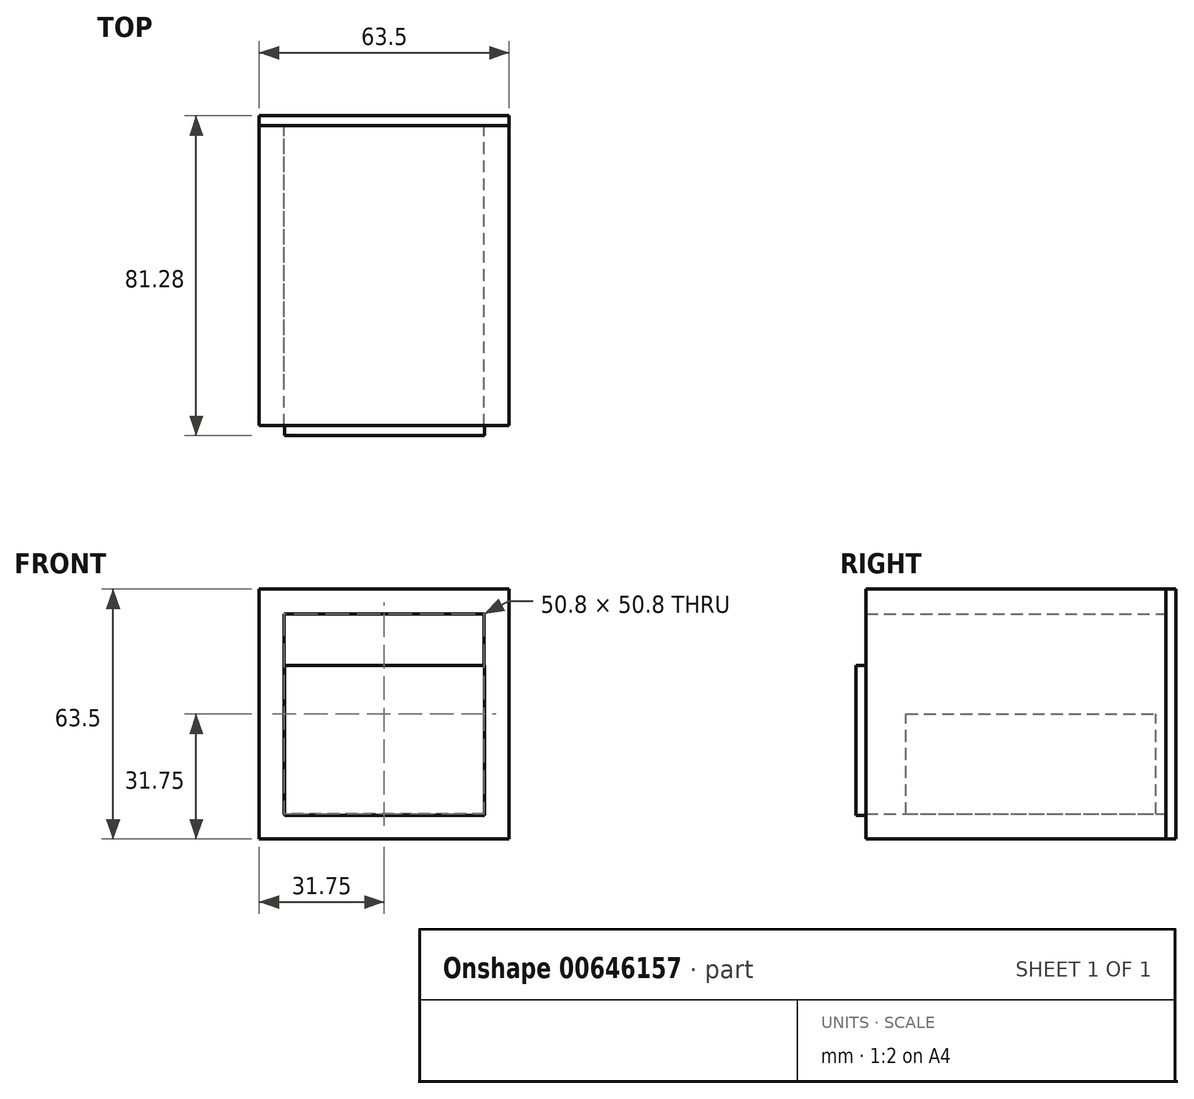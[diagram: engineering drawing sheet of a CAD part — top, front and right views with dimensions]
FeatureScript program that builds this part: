
annotation { "Feature Type Name" : "Feature", "Feature Type Description" : "" }
export const myFeature = defineFeature(function(context is Context, id is Id, definition is map)
    precondition{}
    {
        {
            var Q0;
            Q0=qCreatedBy(makeId("Front.planeOp"),FACE);
            var sketch = newSketch(context, id + "F0", { "sketchPlane" : qUnion([Q0])});
            skLineSegment(sketch, "E0.bottom", {"start": v(25.4, 25.4) * mm, "end": v(-25.4, 25.4) * mm});
            skLineSegment(sketch, "E0.top", {"start": v(25.4, -25.4) * mm, "end": v(-25.4, -25.4) * mm});
            skLineSegment(sketch, "E0.left", {"start": v(25.4, 25.4) * mm, "end": v(25.4, -25.4) * mm});
            skLineSegment(sketch, "E0.right", {"start": v(-25.4, 25.4) * mm, "end": v(-25.4, -25.4) * mm});
            skPoint(sketch, "E0.middle", {"position": v(0, 0) * mm});
            skSolve(sketch);
        }
        {
            var Q0;
            Q0=qCreatedBy(makeId("Front.planeOp"),FACE);
            var sketch = newSketch(context, id + "F1", { "sketchPlane" : qUnion([Q0])});
            skLineSegment(sketch, "E1.bottom", {"start": v(31.75, 31.75) * mm, "end": v(-31.75, 31.75) * mm});
            skLineSegment(sketch, "E1.top", {"start": v(31.75, -31.75) * mm, "end": v(-31.75, -31.75) * mm});
            skLineSegment(sketch, "E1.left", {"start": v(31.75, 31.75) * mm, "end": v(31.75, -31.75) * mm});
            skLineSegment(sketch, "E1.right", {"start": v(-31.75, 31.75) * mm, "end": v(-31.75, -31.75) * mm});
            skPoint(sketch, "E1.middle", {"position": v(0, 0) * mm});
            skSolve(sketch);
        }
        {
            var Q0;
            Q0=makeQuery(id+"F1.imprint","IMPRINT",FACE,{"disambiguationData":[TD([[makeQuery(id+"F1.imprint","IMPRINT",EDGE,{"derivedFrom":sQuery(id+"F1.wireOp",EDGE,"E1.bottom")}),1.0]])]});
            extrude(context, id + "F2", {"entities" : qUnion([Q0]), "depth" : 76.2 * mm, "offsetDistance" : 25.4 * mm});
        }
        {
            var Q0;
            Q0=qCreatedBy(makeId("Front.planeOp"),FACE);
            cPlane(context, id + "F3", {"entities" : qUnion([Q0]), "cplaneType" : CPlaneType.OFFSET, "offset" : 2.54 * mm, "width" : 152.4 * mm, "height" : 152.4 * mm});
        }
        {
            var Q0;
            Q0=qCreatedBy(id+"F3.planeOp",FACE);
            var sketch = newSketch(context, id + "F4", { "sketchPlane" : qUnion([Q0])});
            skLineSegment(sketch, "E2.bottom", {"start": v(-25.47, 0) * mm, "end": v(25.33, 0) * mm});
            skLineSegment(sketch, "E2.top", {"start": v(-25.47, -25.4) * mm, "end": v(25.33, -25.4) * mm});
            skLineSegment(sketch, "E2.left", {"start": v(-25.47, 0) * mm, "end": v(-25.47, -25.4) * mm});
            skLineSegment(sketch, "E2.right", {"start": v(25.33, 0) * mm, "end": v(25.33, -25.4) * mm});
            skSolve(sketch);
        }
        {
            var Q0;
            Q0 = qSketchRegion(id + "F4", true);
            extrude(context, id + "F5", {"entities" : qUnion([Q0]), "depth" : 63.5 * mm, "offsetDistance" : 25.4 * mm});
        }
        {
            var Q0;
            Q0=makeQuery(id+"F2.opExtrude","CAP_FACE",FACE,{"disambiguationData":[OSD([sQuery(id+"F1.wireOp",EDGE,"E1.bottom"),sQuery(id+"F1.wireOp",EDGE,"E1.top"),sQuery(id+"F1.wireOp",EDGE,"E1.left"),sQuery(id+"F1.wireOp",EDGE,"E1.right")])],"isStart":false});
            var sketch = newSketch(context, id + "F6", { "sketchPlane" : qUnion([Q0])});
            skLineSegment(sketch, "E3.bottom", {"start": v(-25.33, 12.34) * mm, "end": v(25.47, 12.34) * mm});
            skLineSegment(sketch, "E3.top", {"start": v(-25.33, -25.76) * mm, "end": v(25.47, -25.76) * mm});
            skLineSegment(sketch, "E3.left", {"start": v(-25.33, 12.34) * mm, "end": v(-25.33, -25.76) * mm});
            skLineSegment(sketch, "E3.right", {"start": v(25.47, 12.34) * mm, "end": v(25.47, -25.76) * mm});
            skSolve(sketch);
        }
        {
            var Q0;
            Q0=makeQuery(id+"F6.imprint","IMPRINT",FACE,{"disambiguationData":[TD([[makeQuery(id+"F6.imprint","IMPRINT",EDGE,{"derivedFrom":sQuery(id+"F6.wireOp",EDGE,"E3.bottom")}),-1.0]])]});
            extrude(context, id + "F7", {"entities" : qUnion([Q0]), "depth" : 2.54 * mm, "offsetDistance" : 25.4 * mm});
        }
        {
            var Q0;
            Q0=makeQuery(id+"F2.opExtrude","CAP_FACE",FACE,{"disambiguationData":[OSD([sQuery(id+"F1.wireOp",EDGE,"E1.bottom"),sQuery(id+"F1.wireOp",EDGE,"E1.top"),sQuery(id+"F1.wireOp",EDGE,"E1.left"),sQuery(id+"F1.wireOp",EDGE,"E1.right")])],"isStart":true});
            extrude(context, id + "F8", {"entities" : qUnion([Q0]), "depth" : 2.54 * mm, "offsetDistance" : 25.4 * mm});
        }
        {
            var Q0;
            Q0 = qSketchRegion(id + "F0", true);
            extrude(context, id + "F9", {"entities" : qUnion([Q0]), "operationType" : NewBodyOperationType.REMOVE, "depth" : 76.2 * mm, "offsetDistance" : 25.4 * mm});
        }
    });
